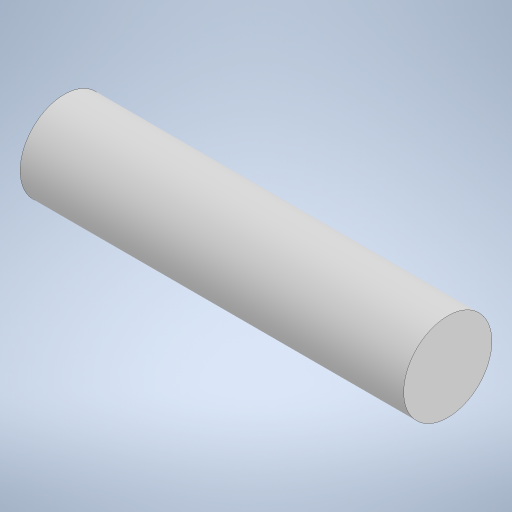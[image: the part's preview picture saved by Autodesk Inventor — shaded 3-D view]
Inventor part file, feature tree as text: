
AUTODESK INVENTOR PART (.ipt)
format: ipt  version: 2023 (Build 270158000, 158)  size: 215,552 bytes
history: native  units: in
note: dims shown in document units (in); Inventor stores cm internally (conversion verified against a paired STEP export)
features: extrude x1, sketch x1
ambient origin geometry x8: Origin, YZ Plane, XZ Plane, XY Plane, X Axis, Y Axis, Z Axis, Center Point
bodies: Solid1 (feature_tree)
feature tree (2):
  extrude  "Extrusion1"  Depth=0.34in TaperAngle=0.0deg
  sketch  "Sketch1"  dims[d0=0.0781in d1=0.34in d2=0.0in]
